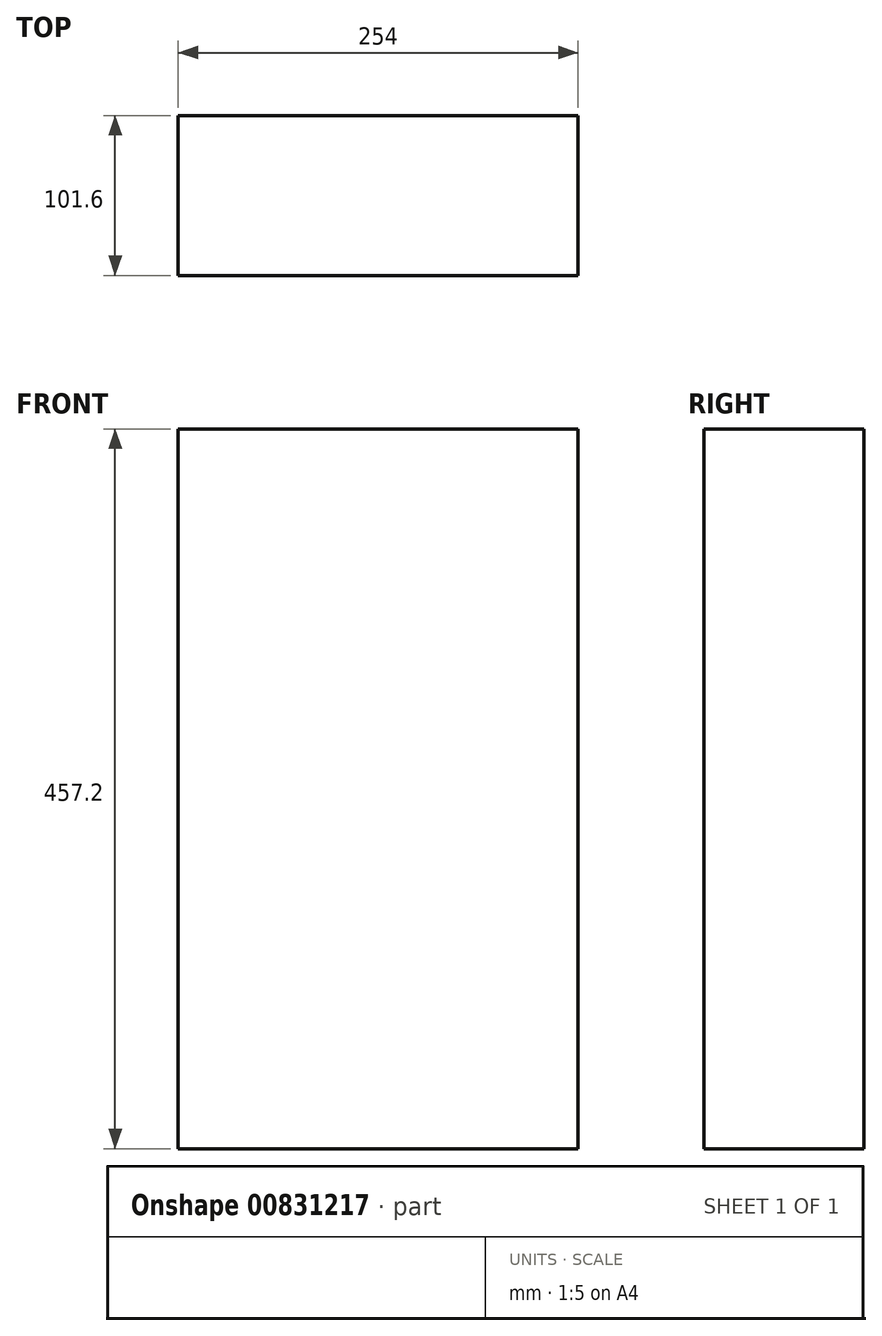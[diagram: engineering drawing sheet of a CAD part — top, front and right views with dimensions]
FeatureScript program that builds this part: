
annotation { "Feature Type Name" : "Feature", "Feature Type Description" : "" }
export const myFeature = defineFeature(function(context is Context, id is Id, definition is map)
    precondition{}
    {
        {
            var Q0;
            Q0=qCreatedBy(makeId("Front.planeOp"),FACE);
            var sketch = newSketch(context, id + "F0", { "sketchPlane" : qUnion([Q0])});
            skLineSegment(sketch, "E0.bottom", {"start": v(127, 228.6) * mm, "end": v(-127, 228.6) * mm});
            skLineSegment(sketch, "E0.top", {"start": v(127, -228.6) * mm, "end": v(-127, -228.6) * mm});
            skLineSegment(sketch, "E0.left", {"start": v(127, 228.6) * mm, "end": v(127, -228.6) * mm});
            skLineSegment(sketch, "E0.right", {"start": v(-127, 228.6) * mm, "end": v(-127, -228.6) * mm});
            skPoint(sketch, "E0.middle", {"position": v(0, 0) * mm});
            skSolve(sketch);
        }
        {
            var Q0;
            Q0=qSketchRegion(id+"F0",true);
            extrude(context, id + "F1", {"entities" : qUnion([Q0]), "depth" : 101.6 * mm, "offsetDistance" : 25.4 * mm});
        }
    });
